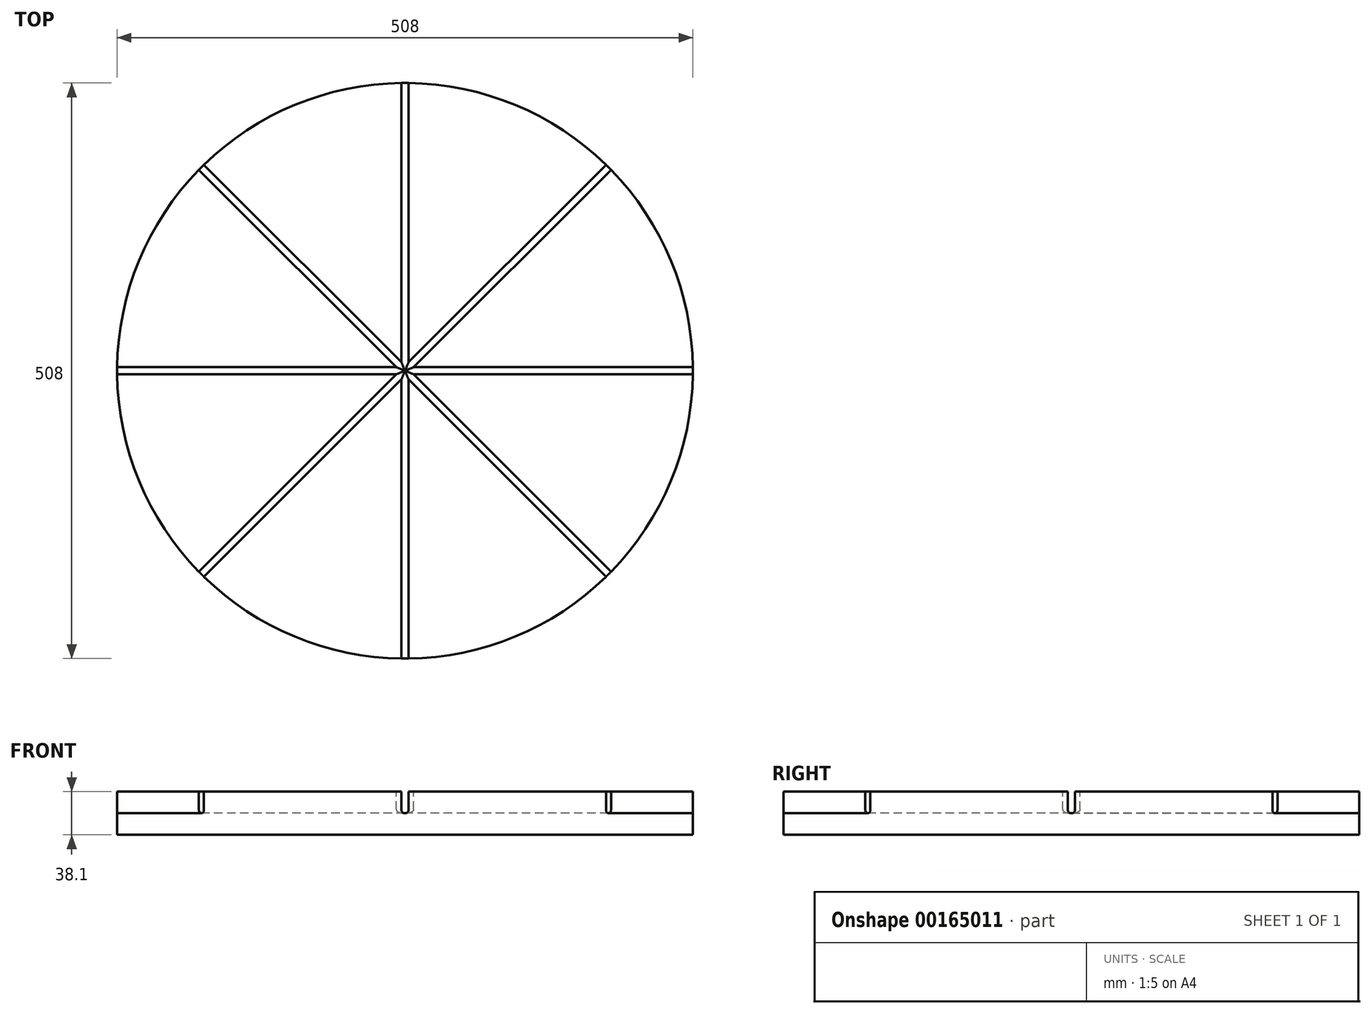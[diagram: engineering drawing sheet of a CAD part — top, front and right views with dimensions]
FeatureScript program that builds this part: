
annotation { "Feature Type Name" : "Feature", "Feature Type Description" : "" }
export const myFeature = defineFeature(function(context is Context, id is Id, definition is map)
    precondition{}
    {
        {
            var Q0;
            Q0=qCreatedBy(makeId("Top.planeOp"),FACE);
            var sketch = newSketch(context, id + "F0", { "sketchPlane" : qUnion([Q0])});
            skCircle(sketch, "E0", {"center": v(0, 0) * mm, "radius": 254 * mm});
            skSolve(sketch);
        }
        {
            var Q0;
            Q0 = qSketchRegion(id + "F0", true);
            extrude(context, id + "F1", {"entities" : qUnion([Q0]), "depth" : 38.1 * mm});
        }
        {
            var Q0;
            Q0=makeQuery(id+"F1.opExtrude","CAP_FACE",FACE,{"disambiguationData":[OSD([sQuery(id+"F0.wireOp",EDGE,"E0")])],"isStart":false});
            var sketch = newSketch(context, id + "F2", { "sketchPlane" : qUnion([Q0])});
            skLineSegment(sketch, "E1.bottom", {"start": v(-3.18, -254) * mm, "end": v(3.17, -254) * mm});
            skLineSegment(sketch, "E1.top", {"start": v(-3.17, 254) * mm, "end": v(3.18, 254) * mm});
            skLineSegment(sketch, "E1.left", {"start": v(-3.18, -254) * mm, "end": v(-3.17, 254) * mm});
            skLineSegment(sketch, "E1.right", {"start": v(3.17, -254) * mm, "end": v(3.18, 254) * mm});
            skPoint(sketch, "E1.middle", {"position": v(0, 0) * mm});
            skLineSegment(sketch, "E2.bottom", {"start": v(-254, -3.18) * mm, "end": v(254, -3.18) * mm});
            skLineSegment(sketch, "E2.top", {"start": v(-254, 3.18) * mm, "end": v(254, 3.18) * mm});
            skLineSegment(sketch, "E2.left", {"start": v(-254, -3.18) * mm, "end": v(-254, 3.18) * mm});
            skLineSegment(sketch, "E2.right", {"start": v(254, -3.18) * mm, "end": v(254, 3.18) * mm});
            skLineSegment(sketch, "E3.bottom", {"start": v(-177.36, 181.85) * mm, "end": v(181.85, -177.36) * mm});
            skLineSegment(sketch, "E3.top", {"start": v(-181.85, 177.36) * mm, "end": v(177.36, -181.85) * mm});
            skLineSegment(sketch, "E3.left", {"start": v(-177.36, 181.85) * mm, "end": v(-181.85, 177.36) * mm});
            skLineSegment(sketch, "E3.right", {"start": v(181.85, -177.36) * mm, "end": v(177.36, -181.85) * mm});
            skLineSegment(sketch, "E4", {"start": v(-3.17, 254) * mm, "end": v(-177.36, 181.85) * mm, "construction": true});
            skLineSegment(sketch, "E5", {"start": v(-181.85, 177.36) * mm, "end": v(-254, 3.17) * mm, "construction": true});
            skLineSegment(sketch, "E6.bottom", {"start": v(-177.36, -181.85) * mm, "end": v(181.85, 177.36) * mm});
            skLineSegment(sketch, "E6.top", {"start": v(-181.85, -177.36) * mm, "end": v(177.36, 181.85) * mm});
            skLineSegment(sketch, "E6.left", {"start": v(-181.85, -177.36) * mm, "end": v(-177.36, -181.85) * mm});
            skLineSegment(sketch, "E6.right", {"start": v(177.36, 181.85) * mm, "end": v(181.85, 177.36) * mm});
            skLineSegment(sketch, "E7", {"start": v(177.36, 181.85) * mm, "end": v(3.17, 254) * mm, "construction": true});
            skLineSegment(sketch, "E8", {"start": v(181.85, 177.36) * mm, "end": v(254, 3.17) * mm, "construction": true});
            skSolve(sketch);
        }
        {
            var Q0;
            Q0 = qSketchRegion(id + "F2", true);
            extrude(context, id + "F3", {"entities" : qUnion([Q0]), "operationType" : NewBodyOperationType.REMOVE, "oppositeDirection" : true, "depth" : 19.05 * mm});
        }
        {
            var Q0;
            {var subQ7=sQuery(id+"F2.wireOp",EDGE,"E2.bottom");var subQ15=sQuery(id+"F2.wireOp",EDGE,"E1.left");var subQ16=makeQuery(id+"F2.imprint","INTERSECT",VERTEX,{"derivedFrom":[subQ15,subQ7]});Q0=makeQuery(id+"F3.boolean.opBoolean","SPLIT",FACE,{"disambiguationData":[TD([makeQuery(id+"F3.opExtrude","SWEPT_FACE",FACE,{"disambiguationData":[OSD([subQ15]),TDD([makeQuery(id+"F2.imprint","IMPRINT",EDGE,{"disambiguationData":[TD([[subQ16,-1.0]])],"derivedFrom":subQ15})])]})])],"derivedFrom":makeQuery(id+"F1.opExtrude","CAP_FACE",FACE,{"disambiguationData":[OSD([sQuery(id+"F0.wireOp",EDGE,"E0")])],"isStart":false})});}
            var Q1;
            Q1=makeQuery(id+"F5.opFillet","SPLIT",FACE,{"disambiguationData":[OD(3.0)],"derivedFrom":makeQuery(id+"F3.boolean.opBoolean","COPY",FACE,{"derivedFrom":makeQuery(id+"F3.opExtrude","CAP_FACE",FACE,{"disambiguationData":[OSD([sQuery(id+"F2.wireOp",EDGE,"E1.bottom"),sQuery(id+"F2.wireOp",EDGE,"E1.top"),sQuery(id+"F2.wireOp",EDGE,"E1.left"),sQuery(id+"F2.wireOp",EDGE,"E1.right"),sQuery(id+"F2.wireOp",EDGE,"E2.bottom"),sQuery(id+"F2.wireOp",EDGE,"E2.top"),sQuery(id+"F2.wireOp",EDGE,"E2.left"),sQuery(id+"F2.wireOp",EDGE,"E2.right"),sQuery(id+"F2.wireOp",EDGE,"E3.bottom"),sQuery(id+"F2.wireOp",EDGE,"E3.top"),sQuery(id+"F2.wireOp",EDGE,"E3.left"),sQuery(id+"F2.wireOp",EDGE,"E3.right"),sQuery(id+"F2.wireOp",EDGE,"E6.bottom"),sQuery(id+"F2.wireOp",EDGE,"E6.top"),sQuery(id+"F2.wireOp",EDGE,"E6.left"),sQuery(id+"F2.wireOp",EDGE,"E6.right")])],"isStart":false})})});
            extrude(context, id + "F4", {"entities" : qUnion([Q0]), "operationType" : NewBodyOperationType.REMOVE, "endBound" : BoundingType.UP_TO_SURFACE, "oppositeDirection" : true, "endBoundEntityFace" : qUnion([Q1]), "depth" : 25.4 * mm});
        }
        {
            var Q0;
            {var subQ0=sQuery(id+"F2.wireOp",EDGE,"E1.right");Q0=makeQuery(id+"F3.boolean.opBoolean","COPY",EDGE,{"derivedFrom":makeQuery(id+"F3.opExtrude","CAP_EDGE",EDGE,{"disambiguationData":[OSD([subQ0]),TDD([makeQuery(id+"F2.imprint","IMPRINT",EDGE,{"disambiguationData":[TD([[makeQuery(id+"F2.imprint","INTERSECT",VERTEX,{"derivedFrom":[subQ0,sQuery(id+"F2.wireOp",EDGE,"E2.top")]}),-1.0]])],"derivedFrom":subQ0}),makeQuery(id+"F2.imprint","IMPRINT",EDGE,{"disambiguationData":[TD([[makeQuery(id+"F2.imprint","INTERSECT",VERTEX,{"derivedFrom":[sQuery(id+"F2.wireOp",EDGE,"E1.top"),subQ0]}),1.0]])],"derivedFrom":subQ0})])],"isStart":false})});}
            var Q1;
            {var subQ0=sQuery(id+"F2.wireOp",EDGE,"E1.left");Q1=makeQuery(id+"F3.boolean.opBoolean","COPY",EDGE,{"derivedFrom":makeQuery(id+"F3.opExtrude","CAP_EDGE",EDGE,{"disambiguationData":[OSD([subQ0]),TDD([makeQuery(id+"F2.imprint","IMPRINT",EDGE,{"disambiguationData":[TD([[makeQuery(id+"F2.imprint","INTERSECT",VERTEX,{"derivedFrom":[subQ0,sQuery(id+"F2.wireOp",EDGE,"E2.top")]}),-1.0]])],"derivedFrom":subQ0}),makeQuery(id+"F2.imprint","IMPRINT",EDGE,{"disambiguationData":[TD([[makeQuery(id+"F2.imprint","INTERSECT",VERTEX,{"derivedFrom":[sQuery(id+"F2.wireOp",EDGE,"E1.top"),subQ0]}),1.0]])],"derivedFrom":subQ0})])],"isStart":false})});}
            var Q2;
            {var subQ0=sQuery(id+"F2.wireOp",EDGE,"E2.top");Q2=makeQuery(id+"F3.boolean.opBoolean","COPY",EDGE,{"derivedFrom":makeQuery(id+"F3.opExtrude","CAP_EDGE",EDGE,{"disambiguationData":[OSD([subQ0]),TDD([makeQuery(id+"F2.imprint","IMPRINT",EDGE,{"disambiguationData":[TD([[makeQuery(id+"F2.imprint","INTERSECT",VERTEX,{"derivedFrom":[subQ0,sQuery(id+"F2.wireOp",EDGE,"E2.left")]}),-1.0]])],"derivedFrom":subQ0}),makeQuery(id+"F2.imprint","IMPRINT",EDGE,{"disambiguationData":[TD([[makeQuery(id+"F2.imprint","INTERSECT",VERTEX,{"derivedFrom":[sQuery(id+"F2.wireOp",EDGE,"E1.left"),subQ0]}),1.0]])],"derivedFrom":subQ0})])],"isStart":false})});}
            var Q3;
            {var subQ0=sQuery(id+"F2.wireOp",EDGE,"E1.left");Q3=makeQuery(id+"F3.boolean.opBoolean","COPY",EDGE,{"derivedFrom":makeQuery(id+"F3.opExtrude","CAP_EDGE",EDGE,{"disambiguationData":[OSD([subQ0]),TDD([makeQuery(id+"F2.imprint","IMPRINT",EDGE,{"disambiguationData":[TD([[makeQuery(id+"F2.imprint","INTERSECT",VERTEX,{"derivedFrom":[sQuery(id+"F2.wireOp",EDGE,"E1.bottom"),subQ0]}),-1.0]])],"derivedFrom":subQ0}),makeQuery(id+"F2.imprint","IMPRINT",EDGE,{"disambiguationData":[TD([[makeQuery(id+"F2.imprint","INTERSECT",VERTEX,{"derivedFrom":[subQ0,sQuery(id+"F2.wireOp",EDGE,"E2.bottom")]}),1.0]])],"derivedFrom":subQ0})])],"isStart":false})});}
            var Q4;
            {var subQ0=sQuery(id+"F2.wireOp",EDGE,"E2.bottom");Q4=makeQuery(id+"F3.boolean.opBoolean","COPY",EDGE,{"derivedFrom":makeQuery(id+"F3.opExtrude","CAP_EDGE",EDGE,{"disambiguationData":[OSD([subQ0]),TDD([makeQuery(id+"F2.imprint","IMPRINT",EDGE,{"disambiguationData":[TD([[makeQuery(id+"F2.imprint","INTERSECT",VERTEX,{"derivedFrom":[subQ0,sQuery(id+"F2.wireOp",EDGE,"E2.left")]}),-1.0]])],"derivedFrom":subQ0}),makeQuery(id+"F2.imprint","IMPRINT",EDGE,{"disambiguationData":[TD([[makeQuery(id+"F2.imprint","INTERSECT",VERTEX,{"derivedFrom":[sQuery(id+"F2.wireOp",EDGE,"E1.left"),subQ0]}),1.0]])],"derivedFrom":subQ0})])],"isStart":false})});}
            var Q5;
            {var subQ0=sQuery(id+"F2.wireOp",EDGE,"E1.right");Q5=makeQuery(id+"F3.boolean.opBoolean","COPY",EDGE,{"derivedFrom":makeQuery(id+"F3.opExtrude","CAP_EDGE",EDGE,{"disambiguationData":[OSD([subQ0]),TDD([makeQuery(id+"F2.imprint","IMPRINT",EDGE,{"disambiguationData":[TD([[makeQuery(id+"F2.imprint","INTERSECT",VERTEX,{"derivedFrom":[sQuery(id+"F2.wireOp",EDGE,"E1.bottom"),subQ0]}),-1.0]])],"derivedFrom":subQ0}),makeQuery(id+"F2.imprint","IMPRINT",EDGE,{"disambiguationData":[TD([[makeQuery(id+"F2.imprint","INTERSECT",VERTEX,{"derivedFrom":[subQ0,sQuery(id+"F2.wireOp",EDGE,"E2.bottom")]}),1.0]])],"derivedFrom":subQ0})])],"isStart":false})});}
            var Q6;
            {var subQ0=sQuery(id+"F2.wireOp",EDGE,"E2.bottom");Q6=makeQuery(id+"F3.boolean.opBoolean","COPY",EDGE,{"derivedFrom":makeQuery(id+"F3.opExtrude","CAP_EDGE",EDGE,{"disambiguationData":[OSD([subQ0]),TDD([makeQuery(id+"F2.imprint","IMPRINT",EDGE,{"disambiguationData":[TD([[makeQuery(id+"F2.imprint","INTERSECT",VERTEX,{"derivedFrom":[sQuery(id+"F2.wireOp",EDGE,"E1.right"),subQ0]}),-1.0]])],"derivedFrom":subQ0}),makeQuery(id+"F2.imprint","IMPRINT",EDGE,{"disambiguationData":[TD([[makeQuery(id+"F2.imprint","INTERSECT",VERTEX,{"derivedFrom":[subQ0,sQuery(id+"F2.wireOp",EDGE,"E2.right")]}),1.0]])],"derivedFrom":subQ0})])],"isStart":false})});}
            var Q7;
            {var subQ0=sQuery(id+"F2.wireOp",EDGE,"E2.top");Q7=makeQuery(id+"F3.boolean.opBoolean","COPY",EDGE,{"derivedFrom":makeQuery(id+"F3.opExtrude","CAP_EDGE",EDGE,{"disambiguationData":[OSD([subQ0]),TDD([makeQuery(id+"F2.imprint","IMPRINT",EDGE,{"disambiguationData":[TD([[makeQuery(id+"F2.imprint","INTERSECT",VERTEX,{"derivedFrom":[sQuery(id+"F2.wireOp",EDGE,"E1.right"),subQ0]}),-1.0]])],"derivedFrom":subQ0}),makeQuery(id+"F2.imprint","IMPRINT",EDGE,{"disambiguationData":[TD([[makeQuery(id+"F2.imprint","INTERSECT",VERTEX,{"derivedFrom":[subQ0,sQuery(id+"F2.wireOp",EDGE,"E2.right")]}),1.0]])],"derivedFrom":subQ0})])],"isStart":false})});}
            var Q8;
            {var subQ0=sQuery(id+"F2.wireOp",EDGE,"E6.top");Q8=makeQuery(id+"F3.boolean.opBoolean","COPY",EDGE,{"derivedFrom":makeQuery(id+"F3.opExtrude","CAP_EDGE",EDGE,{"disambiguationData":[OSD([subQ0]),TDD([makeQuery(id+"F2.imprint","IMPRINT",EDGE,{"disambiguationData":[TD([[makeQuery(id+"F2.imprint","INTERSECT",VERTEX,{"derivedFrom":[sQuery(id+"F2.wireOp",EDGE,"E1.right"),subQ0]}),-1.0]])],"derivedFrom":subQ0}),makeQuery(id+"F2.imprint","IMPRINT",EDGE,{"disambiguationData":[TD([[makeQuery(id+"F2.imprint","INTERSECT",VERTEX,{"derivedFrom":[subQ0,sQuery(id+"F2.wireOp",EDGE,"E6.right")]}),1.0]])],"derivedFrom":subQ0})])],"isStart":false})});}
            var Q9;
            {var subQ0=sQuery(id+"F2.wireOp",EDGE,"E6.bottom");Q9=makeQuery(id+"F3.boolean.opBoolean","COPY",EDGE,{"derivedFrom":makeQuery(id+"F3.opExtrude","CAP_EDGE",EDGE,{"disambiguationData":[OSD([subQ0]),TDD([makeQuery(id+"F2.imprint","IMPRINT",EDGE,{"disambiguationData":[TD([[makeQuery(id+"F2.imprint","INTERSECT",VERTEX,{"derivedFrom":[sQuery(id+"F2.wireOp",EDGE,"E2.top"),subQ0]}),-1.0]])],"derivedFrom":subQ0}),makeQuery(id+"F2.imprint","IMPRINT",EDGE,{"disambiguationData":[TD([[makeQuery(id+"F2.imprint","INTERSECT",VERTEX,{"derivedFrom":[subQ0,sQuery(id+"F2.wireOp",EDGE,"E6.right")]}),1.0]])],"derivedFrom":subQ0})])],"isStart":false})});}
            var Q10;
            {var subQ0=sQuery(id+"F2.wireOp",EDGE,"E6.bottom");Q10=makeQuery(id+"F3.boolean.opBoolean","COPY",EDGE,{"derivedFrom":makeQuery(id+"F3.opExtrude","CAP_EDGE",EDGE,{"disambiguationData":[OSD([subQ0]),TDD([makeQuery(id+"F2.imprint","IMPRINT",EDGE,{"disambiguationData":[TD([[makeQuery(id+"F2.imprint","INTERSECT",VERTEX,{"derivedFrom":[subQ0,sQuery(id+"F2.wireOp",EDGE,"E6.left")]}),-1.0]])],"derivedFrom":subQ0}),makeQuery(id+"F2.imprint","IMPRINT",EDGE,{"disambiguationData":[TD([[makeQuery(id+"F2.imprint","INTERSECT",VERTEX,{"derivedFrom":[sQuery(id+"F2.wireOp",EDGE,"E1.left"),subQ0]}),1.0]])],"derivedFrom":subQ0})])],"isStart":false})});}
            var Q11;
            {var subQ0=sQuery(id+"F2.wireOp",EDGE,"E6.top");Q11=makeQuery(id+"F3.boolean.opBoolean","COPY",EDGE,{"derivedFrom":makeQuery(id+"F3.opExtrude","CAP_EDGE",EDGE,{"disambiguationData":[OSD([subQ0]),TDD([makeQuery(id+"F2.imprint","IMPRINT",EDGE,{"disambiguationData":[TD([[makeQuery(id+"F2.imprint","INTERSECT",VERTEX,{"derivedFrom":[subQ0,sQuery(id+"F2.wireOp",EDGE,"E6.left")]}),-1.0]])],"derivedFrom":subQ0}),makeQuery(id+"F2.imprint","IMPRINT",EDGE,{"disambiguationData":[TD([[makeQuery(id+"F2.imprint","INTERSECT",VERTEX,{"derivedFrom":[sQuery(id+"F2.wireOp",EDGE,"E2.bottom"),subQ0]}),1.0]])],"derivedFrom":subQ0})])],"isStart":false})});}
            var Q12;
            {var subQ0=sQuery(id+"F2.wireOp",EDGE,"E3.top");Q12=makeQuery(id+"F3.boolean.opBoolean","COPY",EDGE,{"derivedFrom":makeQuery(id+"F3.opExtrude","CAP_EDGE",EDGE,{"disambiguationData":[OSD([subQ0]),TDD([makeQuery(id+"F2.imprint","IMPRINT",EDGE,{"disambiguationData":[TD([[makeQuery(id+"F2.imprint","INTERSECT",VERTEX,{"derivedFrom":[subQ0,sQuery(id+"F2.wireOp",EDGE,"E3.left")]}),-1.0]])],"derivedFrom":subQ0}),makeQuery(id+"F2.imprint","IMPRINT",EDGE,{"disambiguationData":[TD([[makeQuery(id+"F2.imprint","INTERSECT",VERTEX,{"derivedFrom":[sQuery(id+"F2.wireOp",EDGE,"E2.top"),subQ0]}),1.0]])],"derivedFrom":subQ0})])],"isStart":false})});}
            var Q13;
            {var subQ0=sQuery(id+"F2.wireOp",EDGE,"E3.bottom");Q13=makeQuery(id+"F3.boolean.opBoolean","COPY",EDGE,{"derivedFrom":makeQuery(id+"F3.opExtrude","CAP_EDGE",EDGE,{"disambiguationData":[OSD([subQ0]),TDD([makeQuery(id+"F2.imprint","IMPRINT",EDGE,{"disambiguationData":[TD([[makeQuery(id+"F2.imprint","INTERSECT",VERTEX,{"derivedFrom":[subQ0,sQuery(id+"F2.wireOp",EDGE,"E3.left")]}),-1.0]])],"derivedFrom":subQ0}),makeQuery(id+"F2.imprint","IMPRINT",EDGE,{"disambiguationData":[TD([[makeQuery(id+"F2.imprint","INTERSECT",VERTEX,{"derivedFrom":[sQuery(id+"F2.wireOp",EDGE,"E1.left"),subQ0]}),1.0]])],"derivedFrom":subQ0})])],"isStart":false})});}
            var Q14;
            {var subQ0=sQuery(id+"F2.wireOp",EDGE,"E3.bottom");Q14=makeQuery(id+"F3.boolean.opBoolean","COPY",EDGE,{"derivedFrom":makeQuery(id+"F3.opExtrude","CAP_EDGE",EDGE,{"disambiguationData":[OSD([subQ0]),TDD([makeQuery(id+"F2.imprint","IMPRINT",EDGE,{"disambiguationData":[TD([[makeQuery(id+"F2.imprint","INTERSECT",VERTEX,{"derivedFrom":[sQuery(id+"F2.wireOp",EDGE,"E2.bottom"),subQ0]}),-1.0]])],"derivedFrom":subQ0}),makeQuery(id+"F2.imprint","IMPRINT",EDGE,{"disambiguationData":[TD([[makeQuery(id+"F2.imprint","INTERSECT",VERTEX,{"derivedFrom":[subQ0,sQuery(id+"F2.wireOp",EDGE,"E3.right")]}),1.0]])],"derivedFrom":subQ0})])],"isStart":false})});}
            var Q15;
            {var subQ0=sQuery(id+"F2.wireOp",EDGE,"E3.top");Q15=makeQuery(id+"F3.boolean.opBoolean","COPY",EDGE,{"derivedFrom":makeQuery(id+"F3.opExtrude","CAP_EDGE",EDGE,{"disambiguationData":[OSD([subQ0]),TDD([makeQuery(id+"F2.imprint","IMPRINT",EDGE,{"disambiguationData":[TD([[makeQuery(id+"F2.imprint","INTERSECT",VERTEX,{"derivedFrom":[sQuery(id+"F2.wireOp",EDGE,"E1.right"),subQ0]}),-1.0]])],"derivedFrom":subQ0}),makeQuery(id+"F2.imprint","IMPRINT",EDGE,{"disambiguationData":[TD([[makeQuery(id+"F2.imprint","INTERSECT",VERTEX,{"derivedFrom":[subQ0,sQuery(id+"F2.wireOp",EDGE,"E3.right")]}),1.0]])],"derivedFrom":subQ0})])],"isStart":false})});}
            fillet(context, id + "F5", {"entities" : qUnion([Q0, Q1, Q2, Q3, Q4, Q5, Q6, Q7, Q8, Q9, Q10, Q11, Q12, Q13, Q14, Q15]), "radius" : 3.17 * mm, "tangentPropagation" : true, "allowEdgeOverflow" : false});
        }
    });
